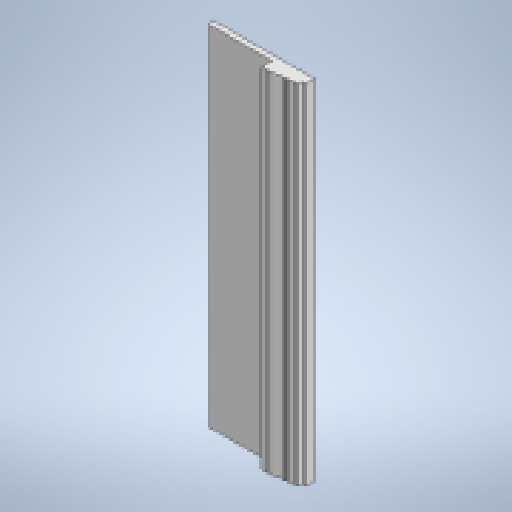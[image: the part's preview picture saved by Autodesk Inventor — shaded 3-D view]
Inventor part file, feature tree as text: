
AUTODESK INVENTOR PART (.ipt)
format: ipt  version: 2023 (Build 270158000, 158)  size: 931,840 bytes
history: native  units: mm
features: extrude x1, sketch x1, other x1
ambient origin geometry x8: Origin, YZ Plane, XZ Plane, XY Plane, X Axis, Y Axis, Z Axis, Center Point
bodies: Solid1 (feature_tree)
feature tree (3):
  extrude  "Extrusion1"  Depth=10.0mm
  sketch  "Sketch1"  dims[d25=609.6mm d26=0.0mm d100=66.085735mm d113=5.0mm d119=30.175621mm d121=20.965007mm d140=18.5mm d144=111.0mm d145=10.0mm d146=7.0mm d147=7.0mm]
  other  "Image2"
